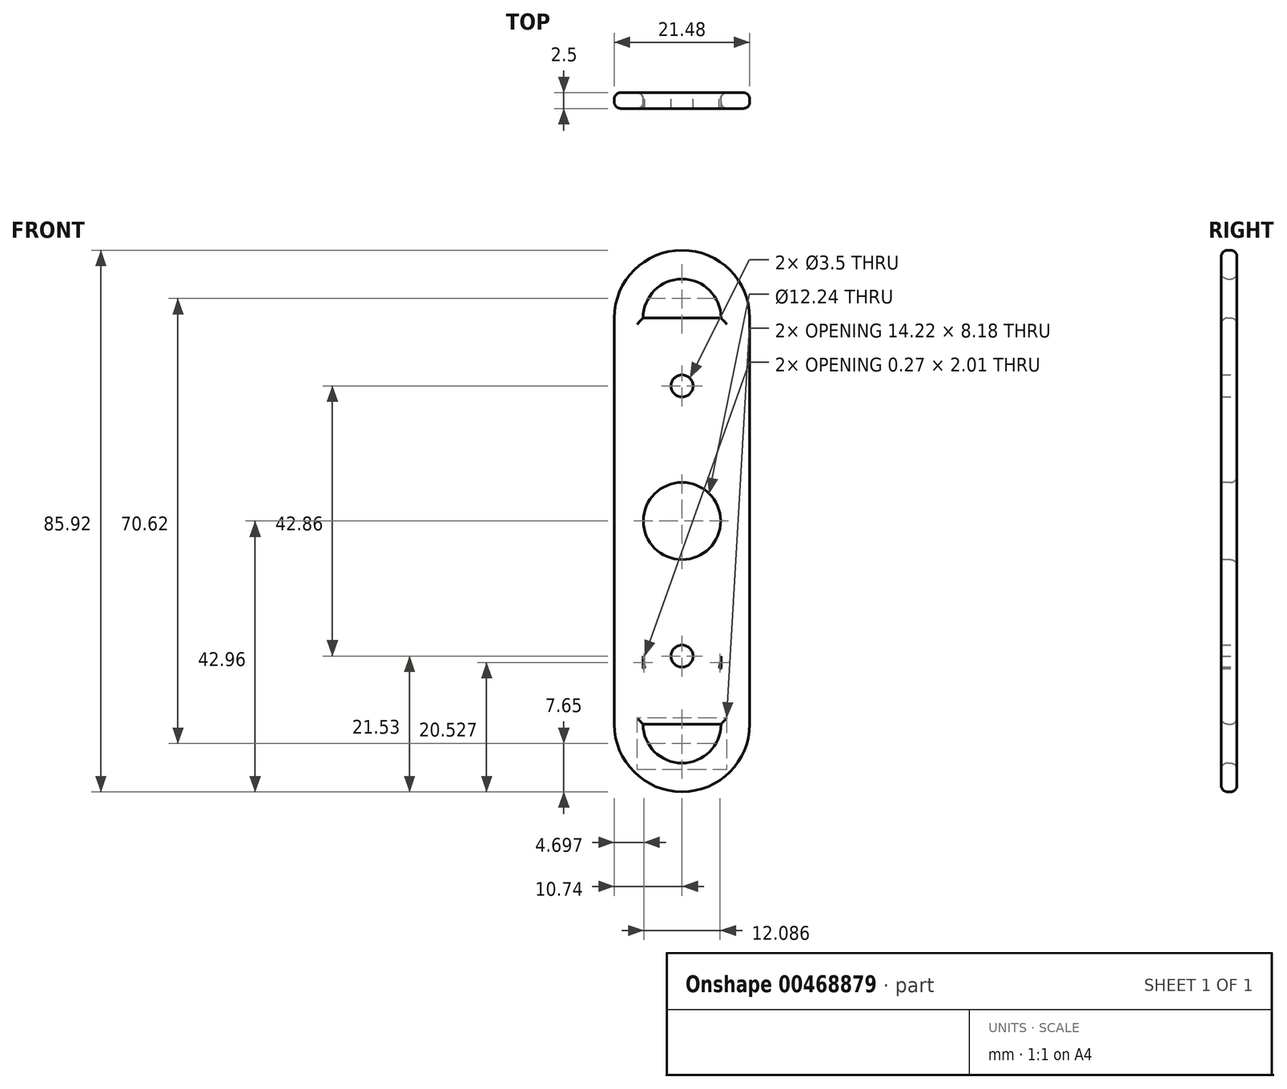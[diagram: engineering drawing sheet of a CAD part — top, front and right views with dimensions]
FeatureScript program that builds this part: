
annotation { "Feature Type Name" : "Feature", "Feature Type Description" : "" }
export const myFeature = defineFeature(function(context is Context, id is Id, definition is map)
    precondition{}
    {
        {
            var Q0;
            Q0=qCreatedBy(makeId("Front.planeOp"),FACE);
            var sketch = newSketch(context, id + "F0", { "sketchPlane" : qUnion([Q0])});
            skLineSegment(sketch, "E0.bottom", {"start": v(6.18, -11.5) * mm, "end": v(-6.18, -11.5) * mm});
            skLineSegment(sketch, "E0.top", {"start": v(6.18, 11.5) * mm, "end": v(-6.18, 11.5) * mm});
            skLineSegment(sketch, "E0.left", {"start": v(6.18, -11.5) * mm, "end": v(6.18, 11.5) * mm});
            skLineSegment(sketch, "E0.right", {"start": v(-6.18, -11.5) * mm, "end": v(-6.18, 11.5) * mm});
            skPoint(sketch, "E0.middle", {"position": v(0, 0) * mm});
            skLineSegment(sketch, "E1.bottom", {"start": v(6.18, -16.1) * mm, "end": v(-6.18, -16.1) * mm});
            skLineSegment(sketch, "E1.top", {"start": v(6.18, 16.1) * mm, "end": v(-6.18, 16.1) * mm});
            skLineSegment(sketch, "E1.left", {"start": v(6.18, -16.1) * mm, "end": v(6.18, 16.1) * mm});
            skLineSegment(sketch, "E1.right", {"start": v(-6.18, -16.1) * mm, "end": v(-6.18, 16.1) * mm});
            skLineSegment(sketch, "E2.left", {"start": v(10.74, -19) * mm, "end": v(10.74, 16.1) * mm});
            skLineSegment(sketch, "E2.right", {"start": v(-10.74, -19) * mm, "end": v(-10.74, 16.1) * mm});
            skLineSegment(sketch, "E3", {"start": v(-6.18, 16.1) * mm, "end": v(6.18, 11.5) * mm, "construction": true});
            skLineSegment(sketch, "E4", {"start": v(-6.18, 11.5) * mm, "end": v(6.18, 16.1) * mm, "construction": true});
            skArc(sketch, "E5", {"start": v(10.74, 16.1) * mm, "mid": v(0, 26.85) * mm, "end": v(-10.74, 16.1) * mm});
            skArc(sketch, "E6", {"start": v(6.18, 16.1) * mm, "mid": v(0, 22.29) * mm, "end": v(-6.18, 16.1) * mm});
            skCircle(sketch, "E7", {"center": v(0, 13.8) * mm, "radius": 1 * mm});
            skCircle(sketch, "E8", {"center": v(0, -13.8) * mm, "radius": 1 * mm});
            skLineSegment(sketch, "E9.bottom", {"start": v(-6.18, -48.33) * mm, "end": v(6.18, -48.33) * mm});
            skLineSegment(sketch, "E9.top", {"start": v(-6.18, -16.1) * mm, "end": v(6.18, -16.1) * mm});
            skLineSegment(sketch, "E9.left", {"start": v(-6.18, -48.33) * mm, "end": v(-6.18, -16.1) * mm});
            skLineSegment(sketch, "E9.right", {"start": v(6.18, -48.33) * mm, "end": v(6.18, -16.1) * mm});
            skLineSegment(sketch, "E10.bottom", {"start": v(6.18, -43.72) * mm, "end": v(-6.18, -43.72) * mm});
            skLineSegment(sketch, "E10.top", {"start": v(6.18, -20.72) * mm, "end": v(-6.18, -20.72) * mm});
            skLineSegment(sketch, "E10.left", {"start": v(6.18, -43.72) * mm, "end": v(6.18, -20.72) * mm});
            skLineSegment(sketch, "E10.right", {"start": v(-6.18, -43.72) * mm, "end": v(-6.18, -20.72) * mm});
            skLineSegment(sketch, "E11", {"start": v(-6.18, -43.72) * mm, "end": v(6.18, -48.33) * mm, "construction": true});
            skLineSegment(sketch, "E12", {"start": v(-6.18, -48.33) * mm, "end": v(6.18, -43.72) * mm, "construction": true});
            skCircle(sketch, "E13", {"center": v(0, -46.03) * mm, "radius": 1 * mm});
            skCircle(sketch, "E14", {"center": v(0, -23.42) * mm, "radius": 1 * mm});
            skPoint(sketch, "E15.center.orphan", {"position": v(0, -48.33) * mm});
            skPoint(sketch, "E16.centerSnap0", {"position": v(0, -16.1) * mm});
            skLineSegment(sketch, "E17", {"start": v(-6.18, -16.1) * mm, "end": v(-6.18, -16.1) * mm});
            skLineSegment(sketch, "E18", {"start": v(6.18, -16.1) * mm, "end": v(6.18, -16.1) * mm});
            skLineSegment(sketch, "E19", {"start": v(-10.74, -19) * mm, "end": v(-10.74, -48.33) * mm});
            skLineSegment(sketch, "E20", {"start": v(10.74, -19) * mm, "end": v(10.74, -48.33) * mm});
            skCircle(sketch, "E21", {"center": v(0, -48.33) * mm, "radius": 6.18 * mm});
            skCircle(sketch, "E22", {"center": v(0, -48.33) * mm, "radius": 10.74 * mm});
            skCircle(sketch, "E23", {"center": v(0, -37.54) * mm, "radius": 6.18 * mm});
            skCircle(sketch, "E24", {"center": v(0, 5.32) * mm, "radius": 6.18 * mm});
            skCircle(sketch, "E25", {"center": v(0, 5.32) * mm, "radius": 1.75 * mm});
            skCircle(sketch, "E26", {"center": v(0, -37.54) * mm, "radius": 1.75 * mm});
            skPoint(sketch, "E27.centerSnap0", {"position": v(6.18, -21.1) * mm});
            skSolve(sketch);
        }
        {
            var Q0;
            {var subQ4=sQuery(id+"F0.wireOp",EDGE,"E22");var subQ15=makeQuery(id+"F0.imprint","INTERSECT",VERTEX,{"derivedFrom":[sQuery(id+"F0.wireOp",EDGE,"E20"),subQ4]});Q0=makeQuery(id+"F0.imprint","IMPRINT",FACE,{"disambiguationData":[TD([[makeQuery(id+"F0.imprint","IMPRINT",EDGE,{"disambiguationData":[TD([[subQ15,-1.0]])],"derivedFrom":subQ4}),1.0]])]});}
            var Q1;
            Q1=makeQuery(id+"F0.imprint","IMPRINT",FACE,{"disambiguationData":[TD([[makeQuery(id+"F0.imprint","IMPRINT",EDGE,{"derivedFrom":sQuery(id+"F0.wireOp",EDGE,"E2.left")}),1.0]])]});
            var Q2;
            {var subQ1=sQuery(id+"F0.wireOp",EDGE,"E0.bottom");Q2=makeQuery(id+"F0.imprint","IMPRINT",FACE,{"disambiguationData":[TD([[makeQuery(id+"F0.imprint","IMPRINT",EDGE,{"derivedFrom":subQ1}),1.0]])]});}
            var Q3;
            {var subQ0=sQuery(id+"F0.wireOp",EDGE,"E0.bottom");Q3=makeQuery(id+"F0.imprint","IMPRINT",FACE,{"disambiguationData":[TD([[makeQuery(id+"F0.imprint","IMPRINT",EDGE,{"derivedFrom":subQ0}),-1.0]])]});}
            var Q4;
            {var subQ0=sQuery(id+"F0.wireOp",EDGE,"E22");var subQ1=sQuery(id+"F0.wireOp",EDGE,"E10.left");var subQ2=makeQuery(id+"F0.imprint","INTERSECT",VERTEX,{"derivedFrom":[subQ1,subQ0]});Q4=makeQuery(id+"F0.imprint","IMPRINT",FACE,{"disambiguationData":[TD([[makeQuery(id+"F0.imprint","IMPRINT",EDGE,{"disambiguationData":[TD([[subQ2,-1.0]])],"derivedFrom":subQ1}),1.0]])]});}
            var Q5;
            {var subQ0=sQuery(id+"F0.wireOp",EDGE,"E10.top");Q5=makeQuery(id+"F0.imprint","IMPRINT",FACE,{"disambiguationData":[TD([[makeQuery(id+"F0.imprint","IMPRINT",EDGE,{"derivedFrom":subQ0}),1.0]])]});}
            var Q6;
            {var subQ5=sQuery(id+"F0.wireOp",EDGE,"E21");var subQ6=sQuery(id+"F0.wireOp",EDGE,"E10.bottom");var subQ7=makeQuery(id+"F0.imprint","INTERSECT",VERTEX,{"disambiguationData":[OD(0.0)],"derivedFrom":[subQ6,subQ5]});Q6=makeQuery(id+"F0.imprint","IMPRINT",FACE,{"disambiguationData":[TD([[makeQuery(id+"F0.imprint","IMPRINT",EDGE,{"disambiguationData":[TD([[subQ7,-1.0]])],"derivedFrom":subQ5}),-1.0]])]});}
            var Q7;
            {var subQ0=sQuery(id+"F0.wireOp",EDGE,"E21");var subQ1=sQuery(id+"F0.wireOp",EDGE,"E10.bottom");var subQ2=makeQuery(id+"F0.imprint","INTERSECT",VERTEX,{"disambiguationData":[OD(0.0)],"derivedFrom":[subQ1,subQ0]});Q7=makeQuery(id+"F0.imprint","IMPRINT",FACE,{"disambiguationData":[TD([[makeQuery(id+"F0.imprint","IMPRINT",EDGE,{"disambiguationData":[TD([[subQ2,-1.0]])],"derivedFrom":subQ1}),-1.0]])]});}
            var Q8;
            {var subQ5=sQuery(id+"F0.wireOp",EDGE,"E9.bottom");Q8=makeQuery(id+"F0.imprint","IMPRINT",FACE,{"disambiguationData":[TD([[makeQuery(id+"F0.imprint","IMPRINT",EDGE,{"derivedFrom":subQ5}),1.0]])]});}
            var Q9;
            {var subQ0=sQuery(id+"F0.wireOp",EDGE,"E21");var subQ3=sQuery(id+"F0.wireOp",EDGE,"E10.bottom");var subQ5=makeQuery(id+"F0.imprint","INTERSECT",VERTEX,{"disambiguationData":[OD(1.0)],"derivedFrom":[subQ3,subQ0]});Q9=makeQuery(id+"F0.imprint","IMPRINT",FACE,{"disambiguationData":[TD([[makeQuery(id+"F0.imprint","IMPRINT",EDGE,{"disambiguationData":[TD([[subQ5,-1.0]])],"derivedFrom":subQ3}),1.0]])]});}
            var Q10;
            {var subQ0=sQuery(id+"F0.wireOp",EDGE,"E21");var subQ3=sQuery(id+"F0.wireOp",EDGE,"E10.bottom");var subQ5=makeQuery(id+"F0.imprint","INTERSECT",VERTEX,{"disambiguationData":[OD(0.0)],"derivedFrom":[subQ3,subQ0]});Q10=makeQuery(id+"F0.imprint","IMPRINT",FACE,{"disambiguationData":[TD([[makeQuery(id+"F0.imprint","IMPRINT",EDGE,{"disambiguationData":[TD([[subQ5,1.0]])],"derivedFrom":subQ3}),1.0]])]});}
            var Q11;
            {var subQ3=sQuery(id+"F0.wireOp",EDGE,"E10.top");Q11=makeQuery(id+"F0.imprint","IMPRINT",FACE,{"disambiguationData":[TD([[makeQuery(id+"F0.imprint","IMPRINT",EDGE,{"derivedFrom":subQ3}),-1.0]])]});}
            var Q12;
            Q12=makeQuery(id+"F0.imprint","IMPRINT",FACE,{"disambiguationData":[TD([[makeQuery(id+"F0.imprint","IMPRINT",EDGE,{"derivedFrom":sQuery(id+"F0.wireOp",EDGE,"E13")}),1.0]])]});
            var Q13;
            {var subQ5=sQuery(id+"F0.wireOp",EDGE,"E21");var subQ6=sQuery(id+"F0.wireOp",EDGE,"E10.bottom");var subQ7=makeQuery(id+"F0.imprint","INTERSECT",VERTEX,{"disambiguationData":[OD(1.0)],"derivedFrom":[subQ6,subQ5]});Q13=makeQuery(id+"F0.imprint","IMPRINT",FACE,{"disambiguationData":[TD([[makeQuery(id+"F0.imprint","IMPRINT",EDGE,{"disambiguationData":[TD([[subQ7,1.0]])],"derivedFrom":subQ5}),-1.0]])]});}
            var Q14;
            {var subQ0=sQuery(id+"F0.wireOp",EDGE,"E23");var subQ1=sQuery(id+"F0.wireOp",EDGE,"E10.bottom");var subQ2=makeQuery(id+"F0.imprint","INTERSECT",VERTEX,{"derivedFrom":[subQ1,subQ0]});Q14=makeQuery(id+"F0.imprint","IMPRINT",FACE,{"disambiguationData":[TD([[makeQuery(id+"F0.imprint","IMPRINT",EDGE,{"disambiguationData":[TD([[subQ2,-1.0]])],"derivedFrom":subQ1}),-1.0]])]});}
            var Q15;
            {var subQ0=sQuery(id+"F0.wireOp",EDGE,"E23");var subQ3=sQuery(id+"F0.wireOp",EDGE,"E22");var subQ8=makeQuery(id+"F0.imprint","INTERSECT",VERTEX,{"disambiguationData":[OD(0.0)],"derivedFrom":[subQ3,subQ0]});Q15=makeQuery(id+"F0.imprint","IMPRINT",FACE,{"disambiguationData":[TD([[makeQuery(id+"F0.imprint","IMPRINT",EDGE,{"disambiguationData":[TD([[subQ8,-1.0]])],"derivedFrom":subQ3}),-1.0]])]});}
            var Q16;
            {var subQ0=sQuery(id+"F0.wireOp",EDGE,"E23");var subQ1=sQuery(id+"F0.wireOp",EDGE,"E21");var subQ9=makeQuery(id+"F0.imprint","INTERSECT",VERTEX,{"disambiguationData":[OD(0.0)],"derivedFrom":[subQ1,subQ0]});Q16=makeQuery(id+"F0.imprint","IMPRINT",FACE,{"disambiguationData":[TD([[makeQuery(id+"F0.imprint","IMPRINT",EDGE,{"disambiguationData":[TD([[subQ9,-1.0]])],"derivedFrom":subQ1}),-1.0]])]});}
            var Q17;
            {var subQ0=sQuery(id+"F0.wireOp",EDGE,"E23");var subQ1=sQuery(id+"F0.wireOp",EDGE,"E21");var subQ2=makeQuery(id+"F0.imprint","INTERSECT",VERTEX,{"disambiguationData":[OD(0.0)],"derivedFrom":[subQ1,subQ0]});Q17=makeQuery(id+"F0.imprint","IMPRINT",FACE,{"disambiguationData":[TD([[makeQuery(id+"F0.imprint","IMPRINT",EDGE,{"disambiguationData":[TD([[subQ2,-1.0]])],"derivedFrom":subQ1}),1.0]])]});}
            var Q18;
            {var subQ0=sQuery(id+"F0.wireOp",EDGE,"E22");var subQ1=sQuery(id+"F0.wireOp",EDGE,"E10.right");var subQ2=makeQuery(id+"F0.imprint","INTERSECT",VERTEX,{"derivedFrom":[subQ1,subQ0]});Q18=makeQuery(id+"F0.imprint","IMPRINT",FACE,{"disambiguationData":[TD([[makeQuery(id+"F0.imprint","IMPRINT",EDGE,{"disambiguationData":[TD([[subQ2,-1.0]])],"derivedFrom":subQ1}),-1.0]])]});}
            var Q19;
            Q19=makeQuery(id+"F0.imprint","IMPRINT",FACE,{"disambiguationData":[TD([[makeQuery(id+"F0.imprint","IMPRINT",EDGE,{"derivedFrom":sQuery(id+"F0.wireOp",EDGE,"E25")}),-1.0]])]});
            var Q20;
            {var subQ0=sQuery(id+"F0.wireOp",EDGE,"E1.right");var subQ1=sQuery(id+"F0.wireOp",EDGE,"E0.top");var subQ2=makeQuery(id+"F0.imprint","INTERSECT",VERTEX,{"derivedFrom":[subQ1,subQ0]});Q20=makeQuery(id+"F0.imprint","IMPRINT",FACE,{"disambiguationData":[TD([[makeQuery(id+"F0.imprint","IMPRINT",EDGE,{"disambiguationData":[TD([[subQ2,1.0]])],"derivedFrom":subQ1}),1.0]])]});}
            var Q21;
            {var subQ4=sQuery(id+"F0.wireOp",EDGE,"E1.top");Q21=makeQuery(id+"F0.imprint","IMPRINT",FACE,{"disambiguationData":[TD([[makeQuery(id+"F0.imprint","IMPRINT",EDGE,{"derivedFrom":subQ4}),1.0]])]});}
            var Q22;
            {var subQ0=sQuery(id+"F0.wireOp",EDGE,"E1.left");var subQ1=sQuery(id+"F0.wireOp",EDGE,"E0.top");var subQ2=makeQuery(id+"F0.imprint","INTERSECT",VERTEX,{"derivedFrom":[subQ1,subQ0]});Q22=makeQuery(id+"F0.imprint","IMPRINT",FACE,{"disambiguationData":[TD([[makeQuery(id+"F0.imprint","IMPRINT",EDGE,{"disambiguationData":[TD([[subQ2,-1.0]])],"derivedFrom":subQ1}),1.0]])]});}
            var Q23;
            Q23=makeQuery(id+"F0.imprint","IMPRINT",FACE,{"disambiguationData":[TD([[makeQuery(id+"F0.imprint","IMPRINT",EDGE,{"derivedFrom":sQuery(id+"F0.wireOp",EDGE,"E7")}),1.0]])]});
            var Q24;
            Q24=makeQuery(id+"F0.imprint","IMPRINT",FACE,{"disambiguationData":[TD([[makeQuery(id+"F0.imprint","IMPRINT",EDGE,{"derivedFrom":sQuery(id+"F0.wireOp",EDGE,"E8")}),1.0]])]});
            var Q25;
            Q25=makeQuery(id+"F0.imprint","IMPRINT",FACE,{"disambiguationData":[TD([[makeQuery(id+"F0.imprint","IMPRINT",EDGE,{"derivedFrom":sQuery(id+"F0.wireOp",EDGE,"E14")}),-1.0]])]});
            var Q26;
            {var subQ0=sQuery(id+"F0.wireOp",EDGE,"E27");var subQ1=sQuery(id+"F0.wireOp",EDGE,"E1.bottom");var subQ2=makeQuery(id+"F0.imprint","INTERSECT",VERTEX,{"disambiguationData":[OD(0.0)],"derivedFrom":[subQ1,subQ0]});Q26=makeQuery(id+"F0.imprint","IMPRINT",FACE,{"disambiguationData":[TD([[makeQuery(id+"F0.imprint","IMPRINT",EDGE,{"disambiguationData":[TD([[subQ2,-1.0]])],"derivedFrom":subQ1}),-1.0]])]});}
            var Q27;
            {var subQ0=sQuery(id+"F0.wireOp",EDGE,"E27");var subQ1=sQuery(id+"F0.wireOp",EDGE,"E9.top");var subQ2=makeQuery(id+"F0.imprint","INTERSECT",VERTEX,{"disambiguationData":[OD(0.0)],"derivedFrom":[subQ1,subQ0]});Q27=makeQuery(id+"F0.imprint","IMPRINT",FACE,{"disambiguationData":[TD([[makeQuery(id+"F0.imprint","IMPRINT",EDGE,{"disambiguationData":[TD([[subQ2,-1.0]])],"derivedFrom":subQ1}),-1.0]])]});}
            var Q28;
            Q28=makeQuery(id+"F0.imprint","IMPRINT",FACE,{"disambiguationData":[TD([[makeQuery(id+"F0.imprint","IMPRINT",EDGE,{"derivedFrom":sQuery(id+"F0.wireOp",EDGE,"E14")}),1.0]])]});
            extrude(context, id + "F1", {"entities" : qUnion([Q0, Q1, Q2, Q3, Q4, Q5, Q6, Q7, Q8, Q9, Q10, Q11, Q12, Q13, Q14, Q15, Q16, Q17, Q18, Q19, Q20, Q21, Q22, Q23, Q24, Q25, Q26, Q27, Q28]), "depth" : 2.5 * mm});
        }
        {
            var Q0;
            Q0=makeQuery(id+"F1.opExtrude","CAP_FACE",FACE,{"disambiguationData":[OSD([sQuery(id+"F0.wireOp",EDGE,"E1.top"),sQuery(id+"F0.wireOp",EDGE,"E2.left"),sQuery(id+"F0.wireOp",EDGE,"E2.right"),sQuery(id+"F0.wireOp",EDGE,"E5"),sQuery(id+"F0.wireOp",EDGE,"E6"),sQuery(id+"F0.wireOp",EDGE,"E9.bottom"),sQuery(id+"F0.wireOp",EDGE,"E19"),sQuery(id+"F0.wireOp",EDGE,"E20"),sQuery(id+"F0.wireOp",EDGE,"E21"),sQuery(id+"F0.wireOp",EDGE,"E22"),sQuery(id+"F0.wireOp",EDGE,"E25"),sQuery(id+"F0.wireOp",EDGE,"E26")])],"isStart":false});
            var sketch = newSketch(context, id + "F2", { "sketchPlane" : qUnion([Q0])});
            skCircle(sketch, "E28", {"center": v(0, -16.1) * mm, "radius": 6.12 * mm});
            skSolve(sketch);
        }
        {
            var Q0;
            Q0=makeQuery(id+"F2.imprint","IMPRINT",FACE,{"disambiguationData":[TD([[makeQuery(id+"F2.imprint","IMPRINT",EDGE,{"derivedFrom":sQuery(id+"F2.wireOp",EDGE,"E28")}),1.0]])]});
            extrude(context, id + "F3", {"entities" : qUnion([Q0]), "operationType" : NewBodyOperationType.REMOVE, "oppositeDirection" : true, "depth" : 25 * mm});
        }
        {
            var Q0;
            Q0=makeQuery(id+"F1.opExtrude","CAP_EDGE",EDGE,{"disambiguationData":[OSD([sQuery(id+"F0.wireOp",EDGE,"E2.left"),sQuery(id+"F0.wireOp",EDGE,"E20")])],"isStart":false});
            var Q1;
            Q1=makeQuery(id+"F1.opExtrude","CAP_EDGE",EDGE,{"disambiguationData":[OSD([sQuery(id+"F0.wireOp",EDGE,"E5")])],"isStart":false});
            var Q2;
            Q2=makeQuery(id+"F3.boolean.opBoolean","COPY",EDGE,{"derivedFrom":makeQuery(id+"F3.opExtrude","CAP_EDGE",EDGE,{"disambiguationData":[OSD([sQuery(id+"F2.wireOp",EDGE,"E28")])],"isStart":true})});
            var Q3;
            Q3=makeQuery(id+"F1.opExtrude","CAP_EDGE",EDGE,{"disambiguationData":[OSD([sQuery(id+"F0.wireOp",EDGE,"E1.top")])],"isStart":false});
            var Q4;
            Q4=makeQuery(id+"F1.opExtrude","CAP_EDGE",EDGE,{"disambiguationData":[OSD([sQuery(id+"F0.wireOp",EDGE,"E6")])],"isStart":false});
            var Q5;
            Q5=makeQuery(id+"F1.opExtrude","CAP_EDGE",EDGE,{"disambiguationData":[OSD([sQuery(id+"F0.wireOp",EDGE,"E9.bottom")])],"isStart":false});
            var Q6;
            Q6=makeQuery(id+"F1.opExtrude","CAP_EDGE",EDGE,{"disambiguationData":[OSD([sQuery(id+"F0.wireOp",EDGE,"E21")])],"isStart":false});
            var Q7;
            Q7=makeQuery(id+"F1.opExtrude","CAP_EDGE",EDGE,{"disambiguationData":[OSD([sQuery(id+"F0.wireOp",EDGE,"E2.right"),sQuery(id+"F0.wireOp",EDGE,"E19")])],"isStart":true});
            var Q8;
            Q8=makeQuery(id+"F1.opExtrude","CAP_EDGE",EDGE,{"disambiguationData":[OSD([sQuery(id+"F0.wireOp",EDGE,"E21")])],"isStart":true});
            var Q9;
            Q9=makeQuery(id+"F1.opExtrude","CAP_EDGE",EDGE,{"disambiguationData":[OSD([sQuery(id+"F0.wireOp",EDGE,"E9.bottom")])],"isStart":true});
            var Q10;
            Q10=makeQuery(id+"F1.opExtrude","CAP_EDGE",EDGE,{"disambiguationData":[OSD([sQuery(id+"F0.wireOp",EDGE,"E6")])],"isStart":true});
            var Q11;
            Q11=makeQuery(id+"F1.opExtrude","CAP_EDGE",EDGE,{"disambiguationData":[OSD([sQuery(id+"F0.wireOp",EDGE,"E1.top")])],"isStart":true});
            var Q12;
            Q12=makeQuery(id+"F3.boolean.opBoolean","INTERSECT",EDGE,{"derivedFrom":[makeQuery(id+"F1.opExtrude","CAP_FACE",FACE,{"disambiguationData":[OSD([sQuery(id+"F0.wireOp",EDGE,"E1.top"),sQuery(id+"F0.wireOp",EDGE,"E2.left"),sQuery(id+"F0.wireOp",EDGE,"E2.right"),sQuery(id+"F0.wireOp",EDGE,"E5"),sQuery(id+"F0.wireOp",EDGE,"E6"),sQuery(id+"F0.wireOp",EDGE,"E9.bottom"),sQuery(id+"F0.wireOp",EDGE,"E19"),sQuery(id+"F0.wireOp",EDGE,"E20"),sQuery(id+"F0.wireOp",EDGE,"E21"),sQuery(id+"F0.wireOp",EDGE,"E22"),sQuery(id+"F0.wireOp",EDGE,"E25"),sQuery(id+"F0.wireOp",EDGE,"E26")])],"isStart":true}),makeQuery(id+"F3.opExtrude","SWEPT_FACE",FACE,{"disambiguationData":[OSD([sQuery(id+"F2.wireOp",EDGE,"E28")])]})]});
            fillet(context, id + "F4", {"entities" : qUnion([Q0, Q1, Q2, Q3, Q4, Q5, Q6, Q7, Q8, Q9, Q10, Q11, Q12]), "radius" : 1 * mm, "tangentPropagation" : true, "allowEdgeOverflow" : false});
        }
    });
